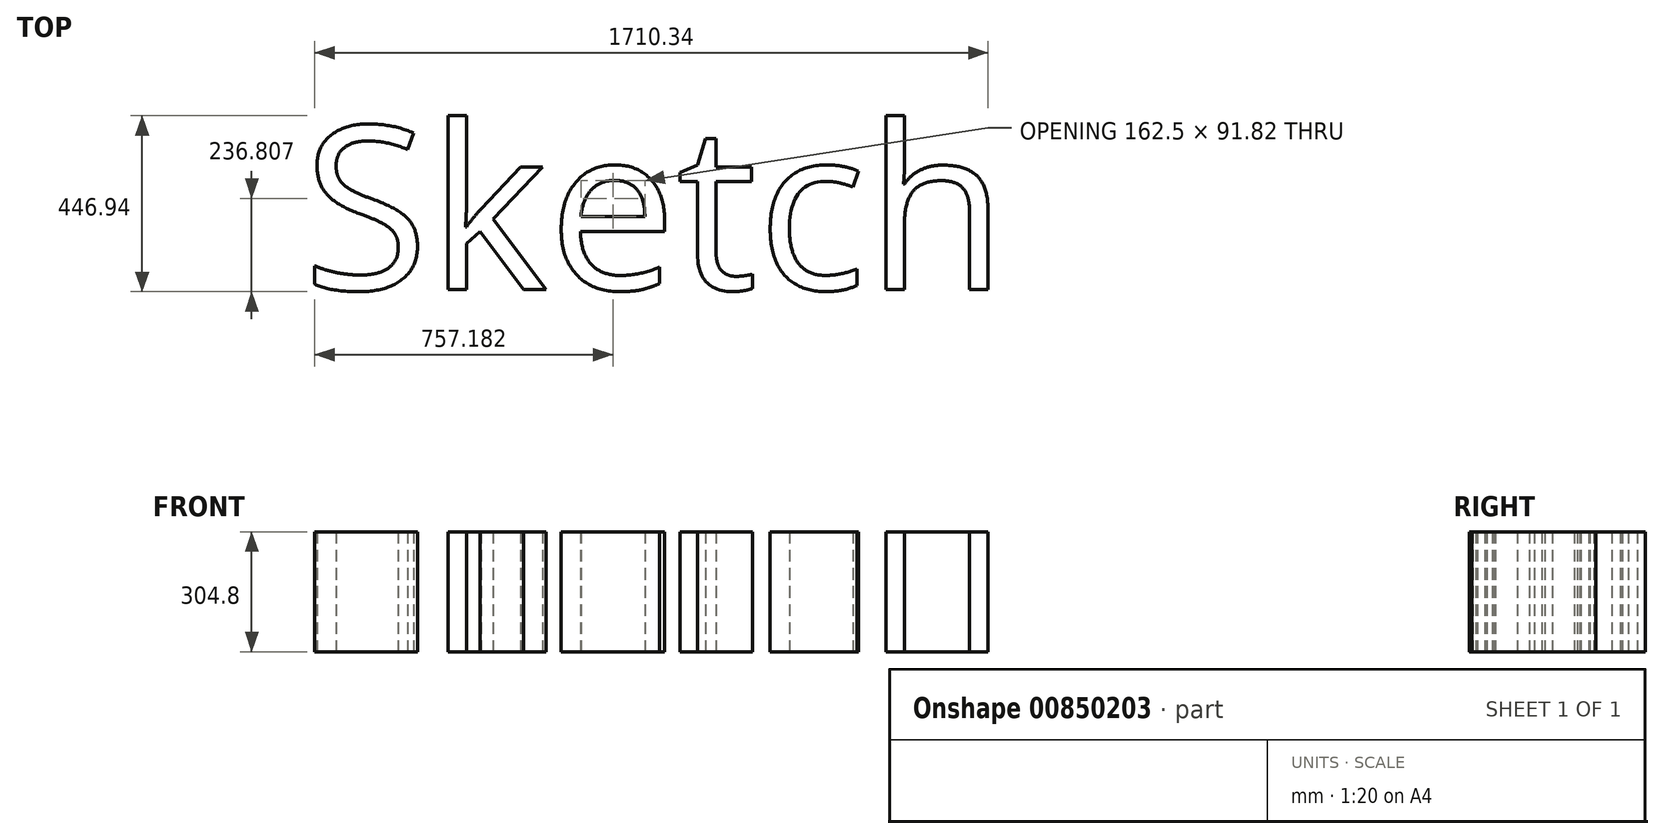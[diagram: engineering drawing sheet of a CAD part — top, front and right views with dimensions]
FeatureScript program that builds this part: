
annotation { "Feature Type Name" : "Feature", "Feature Type Description" : "" }
export const myFeature = defineFeature(function(context is Context, id is Id, definition is map)
    precondition{}
    {
        {
            var Q0;
            Q0=qCreatedBy(makeId("Top.planeOp"),FACE);
            var sketch = newSketch(context, id + "F0", { "sketchPlane" : qUnion([Q0])});
            skText(sketch, "E0", { "text": "Sketch", "fontName": "OpenSans-Regular.ttf"});
            const initialGuessF0  = {"E0": [0.22813, -0.41808, 1, 0, 0.41808]};
            skSetInitialGuess(sketch, initialGuessF0);
            skSolve(sketch);
        }
        {
            var Q0;
            Q0 = qSketchRegion(id + "F0", true);
            extrude(context, id + "F1", {"entities" : qUnion([Q0]), "depth" : 304.8 * mm, "offsetDistance" : 25.4 * mm});
        }
    });
